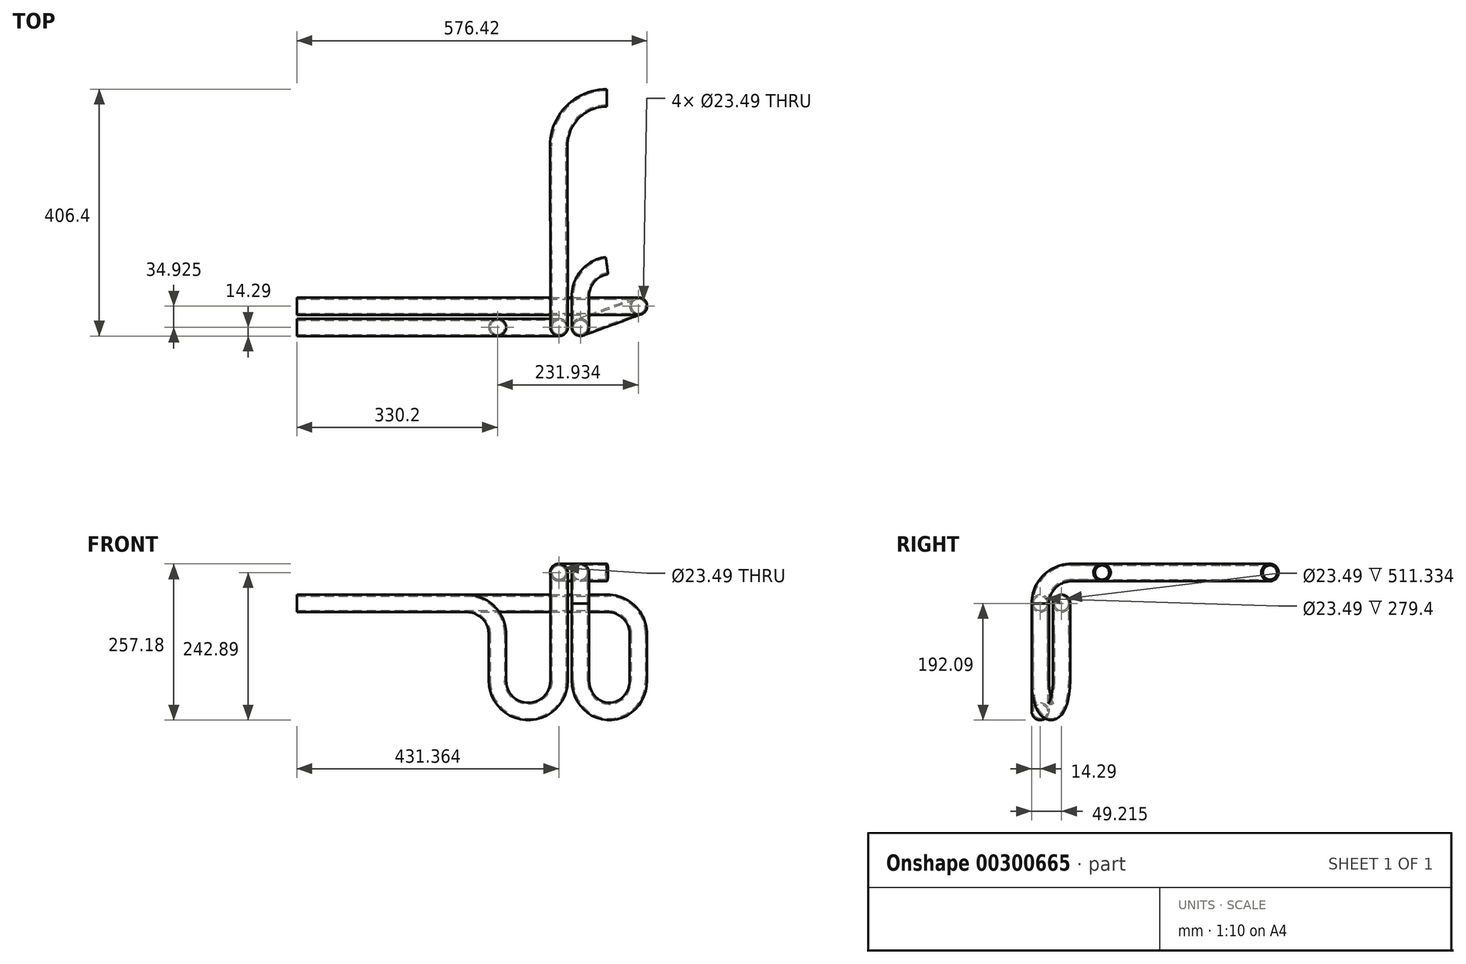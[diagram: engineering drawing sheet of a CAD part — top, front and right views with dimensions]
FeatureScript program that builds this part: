
annotation { "Feature Type Name" : "Feature", "Feature Type Description" : "" }
export const myFeature = defineFeature(function(context is Context, id is Id, definition is map)
    precondition{}
    {
        {
            var Q0;
            Q0=qCreatedBy(makeId("Front.planeOp"),FACE);
            var sketch = newSketch(context, id + "F0", { "sketchPlane" : qUnion([Q0])});
            skLineSegment(sketch, "E0", {"start": v(50.8, -101.6) * mm, "end": v(50.8, -177.8) * mm});
            skArc(sketch, "E1", {"start": v(50.8, -177.8) * mm, "mid": v(101.6, -228.6) * mm, "end": v(152.4, -177.8) * mm});
            skLineSegment(sketch, "E2", {"start": v(152.4, -177.8) * mm, "end": v(152.4, -50.8) * mm});
            skArc(sketch, "E3", {"start": v(50.8, -101.6) * mm, "mid": v(35.92, -65.68) * mm, "end": v(0, -50.8) * mm});
            skLineSegment(sketch, "E4", {"start": v(0, -50.8) * mm, "end": v(-279.4, -50.8) * mm});
            skLineSegment(sketch, "E5", {"start": v(50.8, -177.8) * mm, "end": v(152.4, -177.8) * mm, "construction": true});
            skSolve(sketch);
        }
        {
            var Q0;
            Q0=qCreatedBy(makeId("Top.planeOp"),FACE);
            var sketch = newSketch(context, id + "F1", { "sketchPlane" : qUnion([Q0])});
            skPoint(sketch, "E6.0", {"position": v(152.4, 0) * mm});
            skLineSegment(sketch, "E7", {"start": v(152.4, 0) * mm, "end": v(187.33, 0) * mm, "construction": true});
            skLineSegment(sketch, "E8", {"start": v(187.32, 0) * mm, "end": v(282.73, 34.93) * mm, "construction": true});
            skSolve(sketch);
        }
        {
            var Q0;
            Q0=sQuery(id+"F1.wireOp",EDGE,"E8");
            cPlane(context, id + "F2", {"entities" : qUnion([Q0]), "cplaneType" : CPlaneType.LINE_ANGLE, "offset" : 25.4 * mm, "angle" : 0 * degree, "width" : 152.4 * mm, "height" : 152.4 * mm});
        }
        {
            var Q0;
            Q0=qCreatedBy(id+"F2.planeOp",FACE);
            var sketch = newSketch(context, id + "F3", { "sketchPlane" : qUnion([Q0])});
            skPoint(sketch, "E9.0", {"position": v(-175.9, 0) * mm});
            skLineSegment(sketch, "E10", {"start": v(-175.9, 0) * mm, "end": v(-175.9, -177.8) * mm, "construction": true});
            skPoint(sketch, "E11.0", {"position": v(-143.11, -50.8) * mm});
            skLineSegment(sketch, "E12", {"start": v(-143.11, -50.8) * mm, "end": v(-175.9, -50.8) * mm, "construction": true});
            skLineSegment(sketch, "E13", {"start": v(-175.9, -50.8) * mm, "end": v(-277.5, -50.8) * mm, "construction": true});
            skArc(sketch, "E14", {"start": v(-277.5, -177.8) * mm, "mid": v(-226.7, -228.6) * mm, "end": v(-175.9, -177.8) * mm});
            skLineSegment(sketch, "E15", {"start": v(-175.9, -50.8) * mm, "end": v(-175.9, -177.8) * mm});
            skLineSegment(sketch, "E16", {"start": v(-277.5, -177.8) * mm, "end": v(-277.5, -101.6) * mm});
            skSolve(sketch);
        }
        {
            var Q0;
            Q0=qCreatedBy(makeId("Top.planeOp"),FACE);
            var sketch = newSketch(context, id + "F4", { "sketchPlane" : qUnion([Q0])});
            skPoint(sketch, "E17.0", {"position": v(187.32, 0) * mm});
            skLineSegment(sketch, "E18", {"start": v(187.32, 50.8) * mm, "end": v(187.32, 51.3) * mm});
            skArc(sketch, "E19", {"start": v(231.03, 101.6) * mm, "mid": v(199.78, 84.62) * mm, "end": v(187.32, 51.3) * mm});
            skSolve(sketch);
        }
        {
            var Q0;
            Q0=qCreatedBy(makeId("Right.planeOp"),FACE);
            var Q1;
            Q1=sQuery(id+"F4.wireOp",VERTEX,"E19.end");
            cPlane(context, id + "F5", {"entities" : qUnion([Q0, Q1]), "cplaneType" : CPlaneType.PLANE_POINT, "offset" : 25.4 * mm, "width" : 152.4 * mm, "height" : 152.4 * mm});
        }
        {
            var Q0;
            Q0=qCreatedBy(id+"F5.planeOp",FACE);
            var sketch = newSketch(context, id + "F6", { "sketchPlane" : qUnion([Q0])});
            skPoint(sketch, "E20.0", {"position": v(51.3, 0) * mm});
            skLineSegment(sketch, "E21", {"start": v(51.3, 0) * mm, "end": v(195.28, 0) * mm, "construction": true});
            skPoint(sketch, "E22.0", {"position": v(0, -50.8) * mm});
            skArc(sketch, "E23", {"start": v(51.3, 0) * mm, "mid": v(15.2, -14.85) * mm, "end": v(0, -50.8) * mm});
            skSolve(sketch);
        }
        {
            var Q0;
            Q0=qCreatedBy(makeId("Top.planeOp"),FACE);
            var sketch = newSketch(context, id + "F7", { "sketchPlane" : qUnion([Q0])});
            skPoint(sketch, "E24.0", {"position": v(231.03, 101.6) * mm});
            skPoint(sketch, "E24.1", {"position": v(152.4, 0) * mm});
            skArc(sketch, "E25", {"start": v(231.03, 377.82) * mm, "mid": v(174.83, 354.5) * mm, "end": v(151.66, 298.25) * mm});
            skLineSegment(sketch, "E26", {"start": v(231.03, 101.6) * mm, "end": v(231.03, 377.83) * mm, "construction": true});
            skLineSegment(sketch, "E27", {"start": v(152.27, 50.8) * mm, "end": v(151.66, 298.25) * mm});
            skPoint(sketch, "E28", {"position": v(152.27, 50.8) * mm});
            skSolve(sketch);
        }
        {
            var Q0;
            Q0=sQuery(id+"F7.wireOp",VERTEX,"E28");
            var Q1;
            Q1=sQuery(id+"F1.wireOp",VERTEX,"E6.0");
            var Q2;
            Q2=sQuery(id+"F0.wireOp",VERTEX,"E2.end");
            cPlane(context, id + "F8", {"entities" : qUnion([Q0, Q1, Q2]), "cplaneType" : CPlaneType.THREE_POINT, "offset" : 25.4 * mm, "width" : 152.4 * mm, "height" : 152.4 * mm});
        }
        {
            var Q0;
            Q0=qCreatedBy(id+"F8.planeOp",FACE);
            var sketch = newSketch(context, id + "F9", { "sketchPlane" : qUnion([Q0])});
            skPoint(sketch, "E29.1", {"position": v(-50.42, 0) * mm});
            skPoint(sketch, "E30.0", {"position": v(0.38, -50.8) * mm});
            skLineSegment(sketch, "E31.0", {"start": v(-50.42, 0) * mm, "end": v(-297.87, 0) * mm, "construction": true});
            skLineSegment(sketch, "E31.1", {"start": v(0.38, -177.8) * mm, "end": v(0.38, -50.8) * mm, "construction": true});
            skArc(sketch, "E32", {"start": v(0.38, -50.8) * mm, "mid": v(-14.5, -14.88) * mm, "end": v(-50.42, 0) * mm});
            skSolve(sketch);
        }
        {
            var Q0;
            Q0=qCreatedBy(id+"F5.planeOp",FACE);
            var Q1;
            Q1=sQuery(id+"F6.wireOp",VERTEX,"E22.0");
            cPlane(context, id + "F10", {"entities" : qUnion([Q0, Q1]), "cplaneType" : CPlaneType.PLANE_POINT, "offset" : 25.4 * mm, "width" : 152.4 * mm, "height" : 152.4 * mm});
        }
        {
            var Q0;
            Q0=qCreatedBy(id+"F10.planeOp",FACE);
            var sketch = newSketch(context, id + "F11", { "sketchPlane" : qUnion([Q0])});
            skPoint(sketch, "E33.0", {"position": v(34.93, -50.8) * mm});
            skLineSegment(sketch, "E34", {"start": v(34.93, -50.8) * mm, "end": v(34.93, 0) * mm});
            skPoint(sketch, "E35", {"position": v(34.93, 0) * mm});
            skPoint(sketch, "E36.orphan", {"position": v(34.93, 71) * mm});
            skSolve(sketch);
        }
        {
            var Q0;
            Q0=qCreatedBy(makeId("Front.planeOp"),FACE);
            var Q1;
            Q1=sQuery(id+"F3.wireOp",VERTEX,"E16.end");
            cPlane(context, id + "F12", {"entities" : qUnion([Q0, Q1]), "cplaneType" : CPlaneType.PLANE_POINT, "offset" : 25.4 * mm, "width" : 152.4 * mm, "height" : 152.4 * mm});
        }
        {
            var Q0;
            Q0=qCreatedBy(id+"F12.planeOp",FACE);
            var sketch = newSketch(context, id + "F13", { "sketchPlane" : qUnion([Q0])});
            skLineSegment(sketch, "E37", {"start": v(231.93, -50.8) * mm, "end": v(-279.4, -50.8) * mm});
            skPoint(sketch, "E38.0", {"position": v(-279.4, -50.8) * mm});
            skLineSegment(sketch, "E39", {"start": v(-279.4, -50.8) * mm, "end": v(-279.4, -50.8) * mm});
            skArc(sketch, "E40", {"start": v(282.73, -101.6) * mm, "mid": v(267.85, -65.68) * mm, "end": v(231.93, -50.8) * mm});
            skPoint(sketch, "E41.0", {"position": v(187.32, -50.8) * mm});
            skSolve(sketch);
        }
        {
            var Q0;
            Q0=qCreatedBy(makeId("Right.planeOp"),FACE);
            cPlane(context, id + "F14", {"entities" : qUnion([Q0]), "cplaneType" : CPlaneType.OFFSET, "offset" : 279.4 * mm, "oppositeDirection" : true, "width" : 152.4 * mm, "height" : 152.4 * mm});
        }
        {
            var Q0;
            Q0=qCreatedBy(id+"F14.planeOp",FACE);
            var sketch = newSketch(context, id + "F15", { "sketchPlane" : qUnion([Q0])});
            skPoint(sketch, "E42.0", {"position": v(0, -50.8) * mm});
            skCircle(sketch, "E43", {"center": v(0, -50.8) * mm, "radius": 14.29 * mm});
            skCircle(sketch, "E44.0", {"center": v(0, -50.8) * mm, "radius": 11.75 * mm});
            skSolve(sketch);
        }
        {
            var Q0;
            Q0=qCreatedBy(id+"F14.planeOp",FACE);
            var sketch = newSketch(context, id + "F16", { "sketchPlane" : qUnion([Q0])});
            skPoint(sketch, "E45.0", {"position": v(34.92, -50.8) * mm});
            skCircle(sketch, "E46", {"center": v(34.92, -50.8) * mm, "radius": 14.29 * mm});
            skCircle(sketch, "E47.0", {"center": v(34.92, -50.8) * mm, "radius": 11.75 * mm});
            skSolve(sketch);
        }
        {
            var Q0;
            Q0=makeQuery(id+"F16.imprint","IMPRINT",FACE,{"disambiguationData":[TD([[makeQuery(id+"F16.imprint","IMPRINT",EDGE,{"derivedFrom":sQuery(id+"F16.wireOp",EDGE,"E46")}),1.0]])]});
            var Q1;
            Q1=sQuery(id+"F13.wireOp",EDGE,"E37");
            var Q2;
            Q2=sQuery(id+"F13.wireOp",EDGE,"E40");
            var Q3;
            Q3=sQuery(id+"F3.wireOp",EDGE,"E16");
            var Q4;
            Q4=sQuery(id+"F3.wireOp",EDGE,"E14");
            var Q5;
            Q5=sQuery(id+"F3.wireOp",EDGE,"E15");
            var Q6;
            Q6=sQuery(id+"F6.wireOp",EDGE,"E23");
            var Q7;
            Q7=sQuery(id+"F4.wireOp",EDGE,"E19");
            sweep(context, id + "F17", {"profiles" : qUnion([Q0]), "path" : qUnion([Q1, Q2, Q3, Q4, Q5, Q6, Q7])});
        }
        {
            var Q0;
            Q0=makeQuery(id+"F15.imprint","IMPRINT",FACE,{"disambiguationData":[TD([[makeQuery(id+"F15.imprint","IMPRINT",EDGE,{"derivedFrom":sQuery(id+"F15.wireOp",EDGE,"E43")}),1.0]])]});
            var Q1;
            Q1=sQuery(id+"F0.wireOp",EDGE,"E4");
            var Q2;
            Q2=sQuery(id+"F0.wireOp",EDGE,"E3");
            var Q3;
            Q3=sQuery(id+"F0.wireOp",EDGE,"E0");
            var Q4;
            Q4=sQuery(id+"F0.wireOp",EDGE,"E1");
            var Q5;
            Q5=sQuery(id+"F0.wireOp",EDGE,"E2");
            var Q6;
            Q6=sQuery(id+"F9.wireOp",EDGE,"E32");
            var Q7;
            Q7=sQuery(id+"F7.wireOp",EDGE,"E27");
            var Q8;
            Q8=sQuery(id+"F7.wireOp",EDGE,"E25");
            sweep(context, id + "F18", {"profiles" : qUnion([Q0]), "path" : qUnion([Q1, Q2, Q3, Q4, Q5, Q6, Q7, Q8])});
        }
    });
